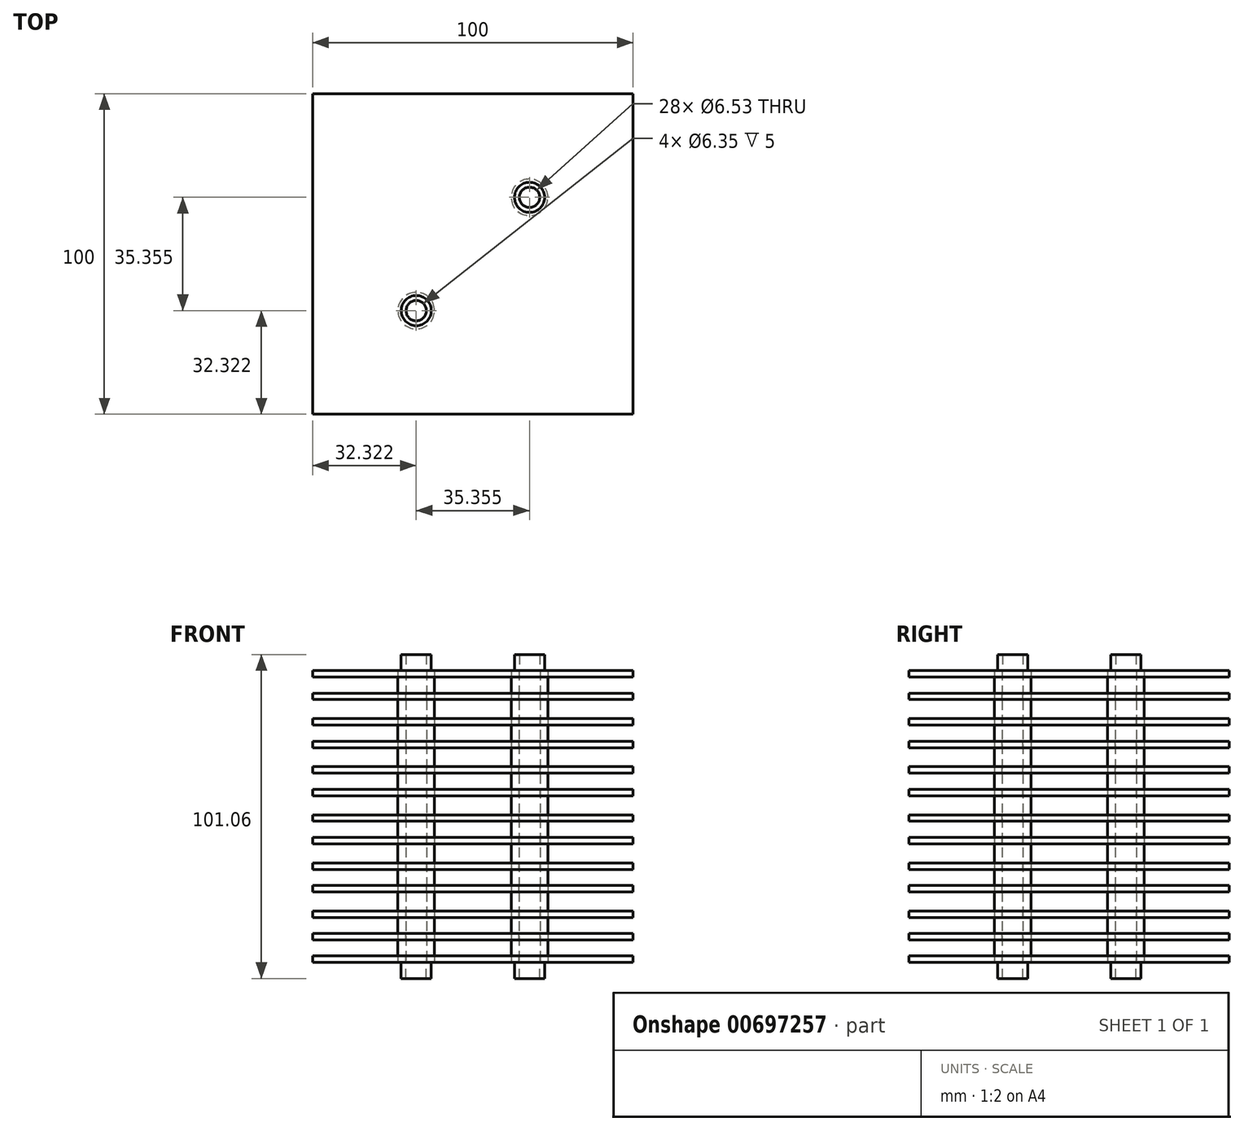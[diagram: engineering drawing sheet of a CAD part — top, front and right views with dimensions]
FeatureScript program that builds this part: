
annotation { "Feature Type Name" : "Feature", "Feature Type Description" : "" }
export const myFeature = defineFeature(function(context is Context, id is Id, definition is map)
    precondition{}
    {
        {
            var Q0;
            Q0=qCreatedBy(makeId("Top.planeOp"),FACE);
            var sketch = newSketch(context, id + "F0", { "sketchPlane" : qUnion([Q0])});
            skLineSegment(sketch, "E0.bottom", {"start": v(50, 50) * mm, "end": v(-50, 50) * mm});
            skLineSegment(sketch, "E0.top", {"start": v(50, -50) * mm, "end": v(-50, -50) * mm});
            skLineSegment(sketch, "E0.left", {"start": v(50, 50) * mm, "end": v(50, -50) * mm});
            skLineSegment(sketch, "E0.right", {"start": v(-50, 50) * mm, "end": v(-50, -50) * mm});
            skPoint(sketch, "E0.middle", {"position": v(0, 0) * mm});
            skLineSegment(sketch, "E1", {"start": v(17.68, 17.68) * mm, "end": v(0, 0) * mm});
            skLineSegment(sketch, "E2", {"start": v(17.68, 17.68) * mm, "end": v(-17.68, -17.68) * mm});
            skCircle(sketch, "E3", {"center": v(-17.68, -17.68) * mm, "radius": 3.27 * mm});
            skCircle(sketch, "E4", {"center": v(17.68, 17.68) * mm, "radius": 3.26 * mm});
            skSolve(sketch);
        }
        {
            var Q0;
            Q0 = qSketchRegion(id + "F0", true);
            extrude(context, id + "F1", {"entities" : qUnion([Q0]), "depth" : 2.02 * mm, "offsetDistance" : 25 * mm});
        }
        {
            var Q0;
            Q0=makeQuery(id+"F1.opExtrude","CAP_FACE",FACE,{"disambiguationData":[OSD([sQuery(id+"F0.wireOp",EDGE,"E0.bottom"),sQuery(id+"F0.wireOp",EDGE,"E0.top"),sQuery(id+"F0.wireOp",EDGE,"E0.left"),sQuery(id+"F0.wireOp",EDGE,"E0.right")])],"isStart":false});
            cPlane(context, id + "F2", {"entities" : qUnion([Q0]), "cplaneType" : CPlaneType.OFFSET, "offset" : 2.5 * mm, "width" : 150 * mm, "height" : 150 * mm});
        }
        {
            var Q0;
            Q0=makeQuery(id+"F1.opExtrude","SWEPT_BODY",BODY,{"disambiguationData":[OSD([sQuery(id+"F0.wireOp",EDGE,"E0.bottom"),sQuery(id+"F0.wireOp",EDGE,"E0.top"),sQuery(id+"F0.wireOp",EDGE,"E0.left"),sQuery(id+"F0.wireOp",EDGE,"E0.right")])]});
            var Q1;
            Q1=qCreatedBy(id+"F2.planeOp",FACE);
            mirror(context, id + "F3", {"entities" : qUnion([Q0]), "mirrorPlane" : qUnion([Q1])});
        }
        {
            var Q0;
            Q0=makeQuery(id+"F3.opPattern","COPY",FACE,{"derivedFrom":makeQuery(id+"F1.opExtrude","CAP_FACE",FACE,{"disambiguationData":[OSD([sQuery(id+"F0.wireOp",EDGE,"E0.bottom"),sQuery(id+"F0.wireOp",EDGE,"E0.top"),sQuery(id+"F0.wireOp",EDGE,"E0.left"),sQuery(id+"F0.wireOp",EDGE,"E0.right")])],"isStart":true}),"instanceName":"1"});
            cPlane(context, id + "F4", {"entities" : qUnion([Q0]), "cplaneType" : CPlaneType.OFFSET, "offset" : 2.5 * mm, "width" : 150 * mm, "height" : 150 * mm});
        }
        {
            var Q0;
            Q0=qCreatedBy(id+"F4.planeOp",FACE);
            cPlane(context, id + "F5", {"entities" : qUnion([Q0]), "cplaneType" : CPlaneType.OFFSET, "offset" : 7.5 * mm, "width" : 150 * mm, "height" : 150 * mm});
        }
        {
            var Q0;
            Q0=qCreatedBy(id+"F5.planeOp",FACE);
            cPlane(context, id + "F6", {"entities" : qUnion([Q0]), "cplaneType" : CPlaneType.OFFSET, "offset" : 7.5 * mm, "width" : 150 * mm, "height" : 150 * mm});
        }
        {
            var Q0;
            Q0=qCreatedBy(id+"F6.planeOp",FACE);
            cPlane(context, id + "F7", {"entities" : qUnion([Q0]), "cplaneType" : CPlaneType.OFFSET, "offset" : 7.5 * mm, "width" : 150 * mm, "height" : 150 * mm});
        }
        {
            var Q0;
            Q0=qCreatedBy(id+"F7.planeOp",FACE);
            cPlane(context, id + "F8", {"entities" : qUnion([Q0]), "cplaneType" : CPlaneType.OFFSET, "offset" : 7.5 * mm, "width" : 150 * mm, "height" : 150 * mm});
        }
        {
            var Q0;
            Q0=qCreatedBy(id+"F8.planeOp",FACE);
            cPlane(context, id + "F9", {"entities" : qUnion([Q0]), "cplaneType" : CPlaneType.OFFSET, "offset" : 7.5 * mm, "width" : 150 * mm, "height" : 150 * mm});
        }
        {
            var Q0;
            Q0=qCreatedBy(id+"F9.planeOp",FACE);
            cPlane(context, id + "F10", {"entities" : qUnion([Q0]), "cplaneType" : CPlaneType.OFFSET, "offset" : 7.5 * mm, "width" : 150 * mm, "height" : 150 * mm});
        }
        {
            var Q0;
            Q0=qCreatedBy(id+"F10.planeOp",FACE);
            cPlane(context, id + "F11", {"entities" : qUnion([Q0]), "cplaneType" : CPlaneType.OFFSET, "offset" : 7.5 * mm, "width" : 150 * mm, "height" : 150 * mm});
        }
        {
            var Q0;
            Q0=qCreatedBy(id+"F11.planeOp",FACE);
            cPlane(context, id + "F12", {"entities" : qUnion([Q0]), "cplaneType" : CPlaneType.OFFSET, "offset" : 7.5 * mm, "width" : 150 * mm, "height" : 150 * mm});
        }
        {
            var Q0;
            Q0=qCreatedBy(id+"F12.planeOp",FACE);
            cPlane(context, id + "F13", {"entities" : qUnion([Q0]), "cplaneType" : CPlaneType.OFFSET, "offset" : 7.5 * mm, "width" : 150 * mm, "height" : 150 * mm});
        }
        {
            var Q0;
            Q0=qCreatedBy(id+"F13.planeOp",FACE);
            cPlane(context, id + "F14", {"entities" : qUnion([Q0]), "cplaneType" : CPlaneType.OFFSET, "offset" : 7.5 * mm, "width" : 150 * mm, "height" : 150 * mm});
        }
        {
            var Q0;
            Q0=makeQuery(id+"F3.opPattern","COPY",BODY,{"derivedFrom":makeQuery(id+"F1.opExtrude","SWEPT_BODY",BODY,{"disambiguationData":[OSD([sQuery(id+"F0.wireOp",EDGE,"E0.bottom"),sQuery(id+"F0.wireOp",EDGE,"E0.top"),sQuery(id+"F0.wireOp",EDGE,"E0.left"),sQuery(id+"F0.wireOp",EDGE,"E0.right")])]}),"instanceName":"1"});
            var Q1;
            Q1=qCreatedBy(id+"F4.planeOp",FACE);
            mirror(context, id + "F15", {"entities" : qUnion([Q0]), "mirrorPlane" : qUnion([Q1])});
        }
        {
            var Q0;
            Q0=makeQuery(id+"F15.opPattern","COPY",BODY,{"derivedFrom":makeQuery(id+"F3.opPattern","COPY",BODY,{"derivedFrom":makeQuery(id+"F1.opExtrude","SWEPT_BODY",BODY,{"disambiguationData":[OSD([sQuery(id+"F0.wireOp",EDGE,"E0.bottom"),sQuery(id+"F0.wireOp",EDGE,"E0.top"),sQuery(id+"F0.wireOp",EDGE,"E0.left"),sQuery(id+"F0.wireOp",EDGE,"E0.right")])]}),"instanceName":"1"}),"instanceName":"1"});
            var Q1;
            Q1=qCreatedBy(id+"F5.planeOp",FACE);
            mirror(context, id + "F16", {"entities" : qUnion([Q0]), "mirrorPlane" : qUnion([Q1])});
        }
        {
            var Q0;
            Q0=makeQuery(id+"F16.opPattern","COPY",BODY,{"derivedFrom":makeQuery(id+"F15.opPattern","COPY",BODY,{"derivedFrom":makeQuery(id+"F3.opPattern","COPY",BODY,{"derivedFrom":makeQuery(id+"F1.opExtrude","SWEPT_BODY",BODY,{"disambiguationData":[OSD([sQuery(id+"F0.wireOp",EDGE,"E0.bottom"),sQuery(id+"F0.wireOp",EDGE,"E0.top"),sQuery(id+"F0.wireOp",EDGE,"E0.left"),sQuery(id+"F0.wireOp",EDGE,"E0.right")])]}),"instanceName":"1"}),"instanceName":"1"}),"instanceName":"1"});
            var Q1;
            Q1=qCreatedBy(id+"F6.planeOp",FACE);
            mirror(context, id + "F17", {"entities" : qUnion([Q0]), "mirrorPlane" : qUnion([Q1])});
        }
        {
            var Q0;
            Q0=makeQuery(id+"F17.opPattern","COPY",BODY,{"derivedFrom":makeQuery(id+"F16.opPattern","COPY",BODY,{"derivedFrom":makeQuery(id+"F15.opPattern","COPY",BODY,{"derivedFrom":makeQuery(id+"F3.opPattern","COPY",BODY,{"derivedFrom":makeQuery(id+"F1.opExtrude","SWEPT_BODY",BODY,{"disambiguationData":[OSD([sQuery(id+"F0.wireOp",EDGE,"E0.bottom"),sQuery(id+"F0.wireOp",EDGE,"E0.top"),sQuery(id+"F0.wireOp",EDGE,"E0.left"),sQuery(id+"F0.wireOp",EDGE,"E0.right")])]}),"instanceName":"1"}),"instanceName":"1"}),"instanceName":"1"}),"instanceName":"1"});
            var Q1;
            Q1=qCreatedBy(id+"F7.planeOp",FACE);
            mirror(context, id + "F18", {"entities" : qUnion([Q0]), "mirrorPlane" : qUnion([Q1])});
        }
        {
            var Q0;
            Q0=makeQuery(id+"F18.opPattern","COPY",BODY,{"derivedFrom":makeQuery(id+"F17.opPattern","COPY",BODY,{"derivedFrom":makeQuery(id+"F16.opPattern","COPY",BODY,{"derivedFrom":makeQuery(id+"F15.opPattern","COPY",BODY,{"derivedFrom":makeQuery(id+"F3.opPattern","COPY",BODY,{"derivedFrom":makeQuery(id+"F1.opExtrude","SWEPT_BODY",BODY,{"disambiguationData":[OSD([sQuery(id+"F0.wireOp",EDGE,"E0.bottom"),sQuery(id+"F0.wireOp",EDGE,"E0.top"),sQuery(id+"F0.wireOp",EDGE,"E0.left"),sQuery(id+"F0.wireOp",EDGE,"E0.right")])]}),"instanceName":"1"}),"instanceName":"1"}),"instanceName":"1"}),"instanceName":"1"}),"instanceName":"1"});
            var Q1;
            Q1=qCreatedBy(id+"F8.planeOp",FACE);
            mirror(context, id + "F19", {"entities" : qUnion([Q0]), "mirrorPlane" : qUnion([Q1])});
        }
        {
            var Q0;
            Q0=makeQuery(id+"F19.opPattern","COPY",BODY,{"derivedFrom":makeQuery(id+"F18.opPattern","COPY",BODY,{"derivedFrom":makeQuery(id+"F17.opPattern","COPY",BODY,{"derivedFrom":makeQuery(id+"F16.opPattern","COPY",BODY,{"derivedFrom":makeQuery(id+"F15.opPattern","COPY",BODY,{"derivedFrom":makeQuery(id+"F3.opPattern","COPY",BODY,{"derivedFrom":makeQuery(id+"F1.opExtrude","SWEPT_BODY",BODY,{"disambiguationData":[OSD([sQuery(id+"F0.wireOp",EDGE,"E0.bottom"),sQuery(id+"F0.wireOp",EDGE,"E0.top"),sQuery(id+"F0.wireOp",EDGE,"E0.left"),sQuery(id+"F0.wireOp",EDGE,"E0.right")])]}),"instanceName":"1"}),"instanceName":"1"}),"instanceName":"1"}),"instanceName":"1"}),"instanceName":"1"}),"instanceName":"1"});
            var Q1;
            Q1=qCreatedBy(id+"F9.planeOp",FACE);
            mirror(context, id + "F20", {"entities" : qUnion([Q0]), "mirrorPlane" : qUnion([Q1])});
        }
        {
            var Q0;
            Q0=makeQuery(id+"F20.opPattern","COPY",BODY,{"derivedFrom":makeQuery(id+"F19.opPattern","COPY",BODY,{"derivedFrom":makeQuery(id+"F18.opPattern","COPY",BODY,{"derivedFrom":makeQuery(id+"F17.opPattern","COPY",BODY,{"derivedFrom":makeQuery(id+"F16.opPattern","COPY",BODY,{"derivedFrom":makeQuery(id+"F15.opPattern","COPY",BODY,{"derivedFrom":makeQuery(id+"F3.opPattern","COPY",BODY,{"derivedFrom":makeQuery(id+"F1.opExtrude","SWEPT_BODY",BODY,{"disambiguationData":[OSD([sQuery(id+"F0.wireOp",EDGE,"E0.bottom"),sQuery(id+"F0.wireOp",EDGE,"E0.top"),sQuery(id+"F0.wireOp",EDGE,"E0.left"),sQuery(id+"F0.wireOp",EDGE,"E0.right")])]}),"instanceName":"1"}),"instanceName":"1"}),"instanceName":"1"}),"instanceName":"1"}),"instanceName":"1"}),"instanceName":"1"}),"instanceName":"1"});
            var Q1;
            Q1=qCreatedBy(id+"F10.planeOp",FACE);
            mirror(context, id + "F21", {"entities" : qUnion([Q0]), "mirrorPlane" : qUnion([Q1])});
        }
        {
            var Q0;
            Q0=makeQuery(id+"F21.opPattern","COPY",BODY,{"derivedFrom":makeQuery(id+"F20.opPattern","COPY",BODY,{"derivedFrom":makeQuery(id+"F19.opPattern","COPY",BODY,{"derivedFrom":makeQuery(id+"F18.opPattern","COPY",BODY,{"derivedFrom":makeQuery(id+"F17.opPattern","COPY",BODY,{"derivedFrom":makeQuery(id+"F16.opPattern","COPY",BODY,{"derivedFrom":makeQuery(id+"F15.opPattern","COPY",BODY,{"derivedFrom":makeQuery(id+"F3.opPattern","COPY",BODY,{"derivedFrom":makeQuery(id+"F1.opExtrude","SWEPT_BODY",BODY,{"disambiguationData":[OSD([sQuery(id+"F0.wireOp",EDGE,"E0.bottom"),sQuery(id+"F0.wireOp",EDGE,"E0.top"),sQuery(id+"F0.wireOp",EDGE,"E0.left"),sQuery(id+"F0.wireOp",EDGE,"E0.right")])]}),"instanceName":"1"}),"instanceName":"1"}),"instanceName":"1"}),"instanceName":"1"}),"instanceName":"1"}),"instanceName":"1"}),"instanceName":"1"}),"instanceName":"1"});
            var Q1;
            Q1=qCreatedBy(id+"F11.planeOp",FACE);
            mirror(context, id + "F22", {"entities" : qUnion([Q0]), "mirrorPlane" : qUnion([Q1])});
        }
        {
            var Q0;
            Q0=makeQuery(id+"F22.opPattern","COPY",BODY,{"derivedFrom":makeQuery(id+"F21.opPattern","COPY",BODY,{"derivedFrom":makeQuery(id+"F20.opPattern","COPY",BODY,{"derivedFrom":makeQuery(id+"F19.opPattern","COPY",BODY,{"derivedFrom":makeQuery(id+"F18.opPattern","COPY",BODY,{"derivedFrom":makeQuery(id+"F17.opPattern","COPY",BODY,{"derivedFrom":makeQuery(id+"F16.opPattern","COPY",BODY,{"derivedFrom":makeQuery(id+"F15.opPattern","COPY",BODY,{"derivedFrom":makeQuery(id+"F3.opPattern","COPY",BODY,{"derivedFrom":makeQuery(id+"F1.opExtrude","SWEPT_BODY",BODY,{"disambiguationData":[OSD([sQuery(id+"F0.wireOp",EDGE,"E0.bottom"),sQuery(id+"F0.wireOp",EDGE,"E0.top"),sQuery(id+"F0.wireOp",EDGE,"E0.left"),sQuery(id+"F0.wireOp",EDGE,"E0.right")])]}),"instanceName":"1"}),"instanceName":"1"}),"instanceName":"1"}),"instanceName":"1"}),"instanceName":"1"}),"instanceName":"1"}),"instanceName":"1"}),"instanceName":"1"}),"instanceName":"1"});
            var Q1;
            Q1=qCreatedBy(id+"F12.planeOp",FACE);
            mirror(context, id + "F23", {"entities" : qUnion([Q0]), "mirrorPlane" : qUnion([Q1])});
        }
        {
            var Q0;
            Q0=makeQuery(id+"F23.opPattern","COPY",BODY,{"derivedFrom":makeQuery(id+"F22.opPattern","COPY",BODY,{"derivedFrom":makeQuery(id+"F21.opPattern","COPY",BODY,{"derivedFrom":makeQuery(id+"F20.opPattern","COPY",BODY,{"derivedFrom":makeQuery(id+"F19.opPattern","COPY",BODY,{"derivedFrom":makeQuery(id+"F18.opPattern","COPY",BODY,{"derivedFrom":makeQuery(id+"F17.opPattern","COPY",BODY,{"derivedFrom":makeQuery(id+"F16.opPattern","COPY",BODY,{"derivedFrom":makeQuery(id+"F15.opPattern","COPY",BODY,{"derivedFrom":makeQuery(id+"F3.opPattern","COPY",BODY,{"derivedFrom":makeQuery(id+"F1.opExtrude","SWEPT_BODY",BODY,{"disambiguationData":[OSD([sQuery(id+"F0.wireOp",EDGE,"E0.bottom"),sQuery(id+"F0.wireOp",EDGE,"E0.top"),sQuery(id+"F0.wireOp",EDGE,"E0.left"),sQuery(id+"F0.wireOp",EDGE,"E0.right")])]}),"instanceName":"1"}),"instanceName":"1"}),"instanceName":"1"}),"instanceName":"1"}),"instanceName":"1"}),"instanceName":"1"}),"instanceName":"1"}),"instanceName":"1"}),"instanceName":"1"}),"instanceName":"1"});
            var Q1;
            Q1=qCreatedBy(id+"F13.planeOp",FACE);
            mirror(context, id + "F24", {"entities" : qUnion([Q0]), "mirrorPlane" : qUnion([Q1])});
        }
        {
            var Q0;
            Q0=makeQuery(id+"F24.opPattern","COPY",BODY,{"derivedFrom":makeQuery(id+"F23.opPattern","COPY",BODY,{"derivedFrom":makeQuery(id+"F22.opPattern","COPY",BODY,{"derivedFrom":makeQuery(id+"F21.opPattern","COPY",BODY,{"derivedFrom":makeQuery(id+"F20.opPattern","COPY",BODY,{"derivedFrom":makeQuery(id+"F19.opPattern","COPY",BODY,{"derivedFrom":makeQuery(id+"F18.opPattern","COPY",BODY,{"derivedFrom":makeQuery(id+"F17.opPattern","COPY",BODY,{"derivedFrom":makeQuery(id+"F16.opPattern","COPY",BODY,{"derivedFrom":makeQuery(id+"F15.opPattern","COPY",BODY,{"derivedFrom":makeQuery(id+"F3.opPattern","COPY",BODY,{"derivedFrom":makeQuery(id+"F1.opExtrude","SWEPT_BODY",BODY,{"disambiguationData":[OSD([sQuery(id+"F0.wireOp",EDGE,"E0.bottom"),sQuery(id+"F0.wireOp",EDGE,"E0.top"),sQuery(id+"F0.wireOp",EDGE,"E0.left"),sQuery(id+"F0.wireOp",EDGE,"E0.right")])]}),"instanceName":"1"}),"instanceName":"1"}),"instanceName":"1"}),"instanceName":"1"}),"instanceName":"1"}),"instanceName":"1"}),"instanceName":"1"}),"instanceName":"1"}),"instanceName":"1"}),"instanceName":"1"}),"instanceName":"1"});
            var Q1;
            Q1=qCreatedBy(id+"F14.planeOp",FACE);
            mirror(context, id + "F25", {"entities" : qUnion([Q0]), "mirrorPlane" : qUnion([Q1])});
        }
        {
            var Q0;
            Q0=makeQuery(id+"F1.opExtrude","CAP_FACE",FACE,{"disambiguationData":[OSD([sQuery(id+"F0.wireOp",EDGE,"E0.bottom"),sQuery(id+"F0.wireOp",EDGE,"E0.top"),sQuery(id+"F0.wireOp",EDGE,"E0.left"),sQuery(id+"F0.wireOp",EDGE,"E0.right")])],"isStart":true});
            var sketch = newSketch(context, id + "F26", { "sketchPlane" : qUnion([Q0])});
            skCircle(sketch, "E5", {"center": v(-17.68, 17.68) * mm, "radius": 3.17 * mm});
            skCircle(sketch, "E6.MirrorC", {"center": v(17.68, -17.68) * mm, "radius": 3.17 * mm});
            skLineSegment(sketch, "E7", {"start": v(-17.68, 17.68) * mm, "end": v(17.68, -17.68) * mm});
            skCircle(sketch, "E8", {"center": v(-17.68, 17.68) * mm, "radius": 4.7 * mm});
            skCircle(sketch, "E9", {"center": v(17.68, -17.68) * mm, "radius": 4.7 * mm});
            skSolve(sketch);
        }
        {
            var Q0;
            Q0=makeQuery(id+"F26.imprint","IMPRINT",FACE,{"disambiguationData":[TD([[makeQuery(id+"F26.imprint","IMPRINT",EDGE,{"derivedFrom":sQuery(id+"F26.wireOp",EDGE,"E5")}),-1.0]])]});
            var Q1;
            Q1=makeQuery(id+"F26.imprint","IMPRINT",FACE,{"disambiguationData":[TD([[makeQuery(id+"F26.imprint","IMPRINT",EDGE,{"derivedFrom":sQuery(id+"F26.wireOp",EDGE,"E6.MirrorC")}),-1.0]])]});
            var Q2;
            Q2=makeQuery(id+"F25.opPattern","COPY",BODY,{"derivedFrom":makeQuery(id+"F24.opPattern","COPY",BODY,{"derivedFrom":makeQuery(id+"F23.opPattern","COPY",BODY,{"derivedFrom":makeQuery(id+"F22.opPattern","COPY",BODY,{"derivedFrom":makeQuery(id+"F21.opPattern","COPY",BODY,{"derivedFrom":makeQuery(id+"F20.opPattern","COPY",BODY,{"derivedFrom":makeQuery(id+"F19.opPattern","COPY",BODY,{"derivedFrom":makeQuery(id+"F18.opPattern","COPY",BODY,{"derivedFrom":makeQuery(id+"F17.opPattern","COPY",BODY,{"derivedFrom":makeQuery(id+"F16.opPattern","COPY",BODY,{"derivedFrom":makeQuery(id+"F15.opPattern","COPY",BODY,{"derivedFrom":makeQuery(id+"F3.opPattern","COPY",BODY,{"derivedFrom":makeQuery(id+"F1.opExtrude","SWEPT_BODY",BODY,{"disambiguationData":[OSD([sQuery(id+"F0.wireOp",EDGE,"E0.bottom"),sQuery(id+"F0.wireOp",EDGE,"E0.top"),sQuery(id+"F0.wireOp",EDGE,"E0.left"),sQuery(id+"F0.wireOp",EDGE,"E0.right")])]}),"instanceName":"1"}),"instanceName":"1"}),"instanceName":"1"}),"instanceName":"1"}),"instanceName":"1"}),"instanceName":"1"}),"instanceName":"1"}),"instanceName":"1"}),"instanceName":"1"}),"instanceName":"1"}),"instanceName":"1"}),"instanceName":"1"});
            extrude(context, id + "F27", {"entities" : qUnion([Q0, Q1]), "operationType" : NewBodyOperationType.ADD, "oppositeDirection" : true, "depth" : 91 * mm, "endBoundEntityBody" : qUnion([Q2]), "offsetDistance" : 25 * mm});
        }
        {
            var Q0;
            Q0=makeQuery(id+"F25.opPattern","COPY",FACE,{"derivedFrom":makeQuery(id+"F24.opPattern","COPY",FACE,{"derivedFrom":makeQuery(id+"F23.opPattern","COPY",FACE,{"derivedFrom":makeQuery(id+"F22.opPattern","COPY",FACE,{"derivedFrom":makeQuery(id+"F21.opPattern","COPY",FACE,{"derivedFrom":makeQuery(id+"F20.opPattern","COPY",FACE,{"derivedFrom":makeQuery(id+"F19.opPattern","COPY",FACE,{"derivedFrom":makeQuery(id+"F18.opPattern","COPY",FACE,{"derivedFrom":makeQuery(id+"F17.opPattern","COPY",FACE,{"derivedFrom":makeQuery(id+"F16.opPattern","COPY",FACE,{"derivedFrom":makeQuery(id+"F15.opPattern","COPY",FACE,{"derivedFrom":makeQuery(id+"F3.opPattern","COPY",FACE,{"derivedFrom":makeQuery(id+"F1.opExtrude","CAP_FACE",FACE,{"disambiguationData":[OSD([sQuery(id+"F0.wireOp",EDGE,"E0.bottom"),sQuery(id+"F0.wireOp",EDGE,"E0.top"),sQuery(id+"F0.wireOp",EDGE,"E0.left"),sQuery(id+"F0.wireOp",EDGE,"E0.right")])],"isStart":false}),"instanceName":"1"}),"instanceName":"1"}),"instanceName":"1"}),"instanceName":"1"}),"instanceName":"1"}),"instanceName":"1"}),"instanceName":"1"}),"instanceName":"1"}),"instanceName":"1"}),"instanceName":"1"}),"instanceName":"1"}),"instanceName":"1"});
            var sketch = newSketch(context, id + "F28", { "sketchPlane" : qUnion([Q0])});
            skLineSegment(sketch, "E10", {"start": v(0, 0) * mm, "end": v(-17.68, -17.68) * mm});
            skLineSegment(sketch, "E11", {"start": v(-17.68, -17.68) * mm, "end": v(17.68, 17.68) * mm});
            skCircle(sketch, "E12", {"center": v(17.68, 17.68) * mm, "radius": 3.27 * mm});
            skCircle(sketch, "E13", {"center": v(-17.68, -17.68) * mm, "radius": 3.27 * mm});
            skSolve(sketch);
        }
        {
            var Q0;
            Q0 = qSketchRegion(id + "F28", true);
            extrude(context, id + "F29", {"entities" : qUnion([Q0]), "operationType" : NewBodyOperationType.REMOVE, "endBound" : BoundingType.THROUGH_ALL, "oppositeDirection" : true, "depth" : 100 * mm, "offsetDistance" : 25 * mm});
        }
        {
            var Q0;
            {var subQ0=sQuery(id+"F0.wireOp",EDGE,"E4");var subQ1=sQuery(id+"F0.wireOp",EDGE,"E3");Q0=makeQuery(id+"F27.boolean.opBoolean","MERGE",FACE,{"derivedFrom":[makeQuery(id+"F1.opExtrude","CAP_FACE",FACE,{"disambiguationData":[OSD([sQuery(id+"F0.wireOp",EDGE,"E0.bottom"),sQuery(id+"F0.wireOp",EDGE,"E0.top"),sQuery(id+"F0.wireOp",EDGE,"E0.left"),sQuery(id+"F0.wireOp",EDGE,"E0.right"),subQ1,subQ0])],"isStart":true}),makeQuery(id+"F27.opExtrude","CAP_FACE",FACE,{"disambiguationData":[OSD([subQ1,sQuery(id+"F26.wireOp",EDGE,"E5")])],"isStart":true}),makeQuery(id+"F27.opExtrude","CAP_FACE",FACE,{"disambiguationData":[OSD([subQ0,sQuery(id+"F26.wireOp",EDGE,"E6.MirrorC")])],"isStart":true})]});}
            var sketch = newSketch(context, id + "F30", { "sketchPlane" : qUnion([Q0])});
            skCircle(sketch, "E14", {"center": v(-17.68, 17.68) * mm, "radius": 5.71 * mm});
            skCircle(sketch, "E15", {"center": v(-17.68, 17.68) * mm, "radius": 3.27 * mm});
            skCircle(sketch, "E16", {"center": v(17.68, -17.68) * mm, "radius": 5.71 * mm});
            skCircle(sketch, "E17", {"center": v(17.68, -17.68) * mm, "radius": 3.27 * mm});
            skSolve(sketch);
        }
        {
            var Q0;
            Q0 = qSketchRegion(id + "F30", true);
            extrude(context, id + "F31", {"entities" : qUnion([Q0]), "oppositeDirection" : true, "depth" : 91 * mm, "offsetDistance" : 25 * mm});
        }
        {
            var Q0;
            {var subQ0=sQuery(id+"F0.wireOp",EDGE,"E4");var subQ1=sQuery(id+"F0.wireOp",EDGE,"E3");Q0=makeQuery(id+"F27.boolean.opBoolean","MERGE",FACE,{"derivedFrom":[makeQuery(id+"F1.opExtrude","CAP_FACE",FACE,{"disambiguationData":[OSD([sQuery(id+"F0.wireOp",EDGE,"E0.bottom"),sQuery(id+"F0.wireOp",EDGE,"E0.top"),sQuery(id+"F0.wireOp",EDGE,"E0.left"),sQuery(id+"F0.wireOp",EDGE,"E0.right"),subQ1,subQ0])],"isStart":true}),makeQuery(id+"F27.opExtrude","CAP_FACE",FACE,{"disambiguationData":[OSD([subQ1,sQuery(id+"F26.wireOp",EDGE,"E5")])],"isStart":true}),makeQuery(id+"F27.opExtrude","CAP_FACE",FACE,{"disambiguationData":[OSD([subQ0,sQuery(id+"F26.wireOp",EDGE,"E6.MirrorC")])],"isStart":true})]});}
            var sketch = newSketch(context, id + "F32", { "sketchPlane" : qUnion([Q0])});
            skCircle(sketch, "E18", {"center": v(17.68, -17.68) * mm, "radius": 3.17 * mm});
            skCircle(sketch, "E19", {"center": v(17.68, -17.68) * mm, "radius": 4.7 * mm});
            skCircle(sketch, "E20", {"center": v(-17.68, 17.68) * mm, "radius": 3.17 * mm});
            skCircle(sketch, "E21", {"center": v(-17.68, 17.68) * mm, "radius": 4.7 * mm});
            skSolve(sketch);
        }
        {
            var Q0;
            Q0 = qSketchRegion(id + "F32", true);
            extrude(context, id + "F33", {"entities" : qUnion([Q0]), "depth" : 5 * mm, "offsetDistance" : 25 * mm});
        }
        {
            var Q0;
            Q0=makeQuery(id+"F25.opPattern","COPY",FACE,{"derivedFrom":makeQuery(id+"F24.opPattern","COPY",FACE,{"derivedFrom":makeQuery(id+"F23.opPattern","COPY",FACE,{"derivedFrom":makeQuery(id+"F22.opPattern","COPY",FACE,{"derivedFrom":makeQuery(id+"F21.opPattern","COPY",FACE,{"derivedFrom":makeQuery(id+"F20.opPattern","COPY",FACE,{"derivedFrom":makeQuery(id+"F19.opPattern","COPY",FACE,{"derivedFrom":makeQuery(id+"F18.opPattern","COPY",FACE,{"derivedFrom":makeQuery(id+"F17.opPattern","COPY",FACE,{"derivedFrom":makeQuery(id+"F16.opPattern","COPY",FACE,{"derivedFrom":makeQuery(id+"F15.opPattern","COPY",FACE,{"derivedFrom":makeQuery(id+"F3.opPattern","COPY",FACE,{"derivedFrom":makeQuery(id+"F1.opExtrude","CAP_FACE",FACE,{"disambiguationData":[OSD([sQuery(id+"F0.wireOp",EDGE,"E0.bottom"),sQuery(id+"F0.wireOp",EDGE,"E0.top"),sQuery(id+"F0.wireOp",EDGE,"E0.left"),sQuery(id+"F0.wireOp",EDGE,"E0.right"),sQuery(id+"F0.wireOp",EDGE,"E3"),sQuery(id+"F0.wireOp",EDGE,"E4")])],"isStart":false}),"instanceName":"1"}),"instanceName":"1"}),"instanceName":"1"}),"instanceName":"1"}),"instanceName":"1"}),"instanceName":"1"}),"instanceName":"1"}),"instanceName":"1"}),"instanceName":"1"}),"instanceName":"1"}),"instanceName":"1"}),"instanceName":"1"});
            var sketch = newSketch(context, id + "F34", { "sketchPlane" : qUnion([Q0])});
            skCircle(sketch, "E22", {"center": v(17.68, 17.68) * mm, "radius": 3.17 * mm});
            skCircle(sketch, "E23", {"center": v(17.68, 17.68) * mm, "radius": 4.7 * mm});
            skCircle(sketch, "E24", {"center": v(-17.68, -17.68) * mm, "radius": 3.17 * mm});
            skCircle(sketch, "E25", {"center": v(-17.68, -17.68) * mm, "radius": 4.7 * mm});
            skSolve(sketch);
        }
        {
            var Q0;
            Q0 = qSketchRegion(id + "F34", true);
            extrude(context, id + "F35", {"entities" : qUnion([Q0]), "depth" : 5 * mm, "offsetDistance" : 25 * mm});
        }
    });
